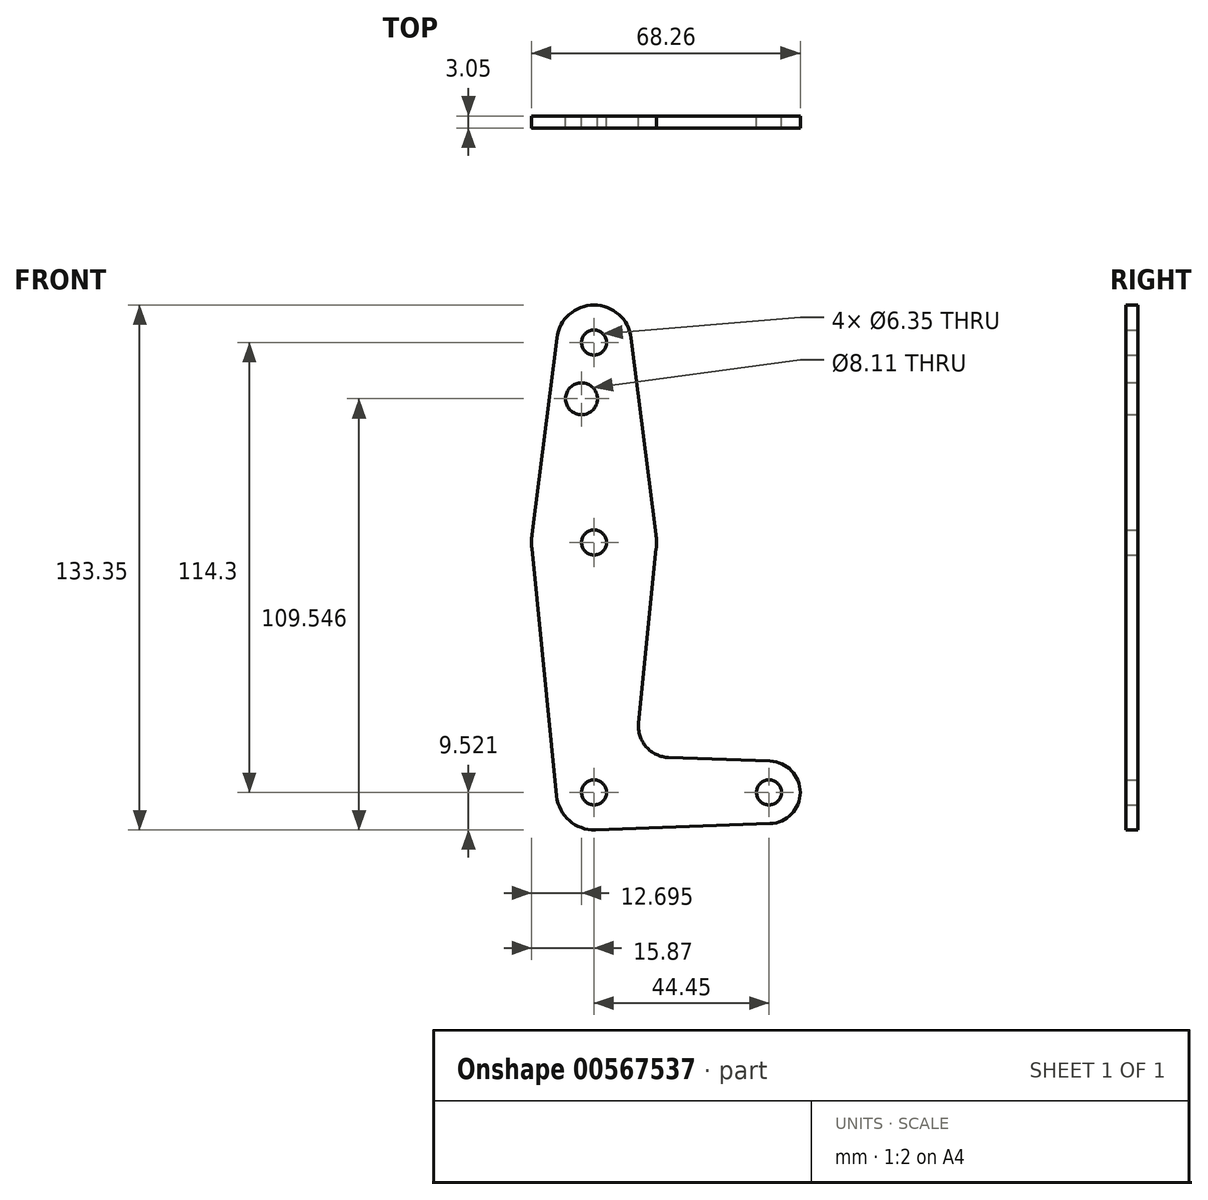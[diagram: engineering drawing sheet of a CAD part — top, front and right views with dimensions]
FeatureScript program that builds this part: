
annotation { "Feature Type Name" : "Feature", "Feature Type Description" : "" }
export const myFeature = defineFeature(function(context is Context, id is Id, definition is map)
    precondition{}
    {
        {
            var Q0;
            Q0=qCreatedBy(makeId("Front.planeOp"),FACE);
            var sketch = newSketch(context, id + "F0", { "sketchPlane" : qUnion([Q0])});
            skLineSegment(sketch, "E0", {"start": v(0, 66.21) * mm, "end": v(0, -48.09) * mm});
            skLineSegment(sketch, "E1", {"start": v(0, -48.09) * mm, "end": v(44.45, -48.09) * mm});
            skCircle(sketch, "E2", {"center": v(0, 66.21) * mm, "radius": 9.53 * mm});
            skCircle(sketch, "E3", {"center": v(0, 15.41) * mm, "radius": 15.88 * mm});
            skCircle(sketch, "E4", {"center": v(0, -48.09) * mm, "radius": 9.53 * mm});
            skCircle(sketch, "E5", {"center": v(44.45, -48.09) * mm, "radius": 7.94 * mm});
            skLineSegment(sketch, "E6", {"start": v(0.34, -57.6) * mm, "end": v(44.73, -56.02) * mm});
            skCircle(sketch, "E7", {"center": v(0, 66.21) * mm, "radius": 3.18 * mm});
            skCircle(sketch, "E8", {"center": v(-3.17, 51.94) * mm, "radius": 4.05 * mm});
            skCircle(sketch, "E9", {"center": v(0, 15.41) * mm, "radius": 3.18 * mm});
            skCircle(sketch, "E10", {"center": v(0, -48.09) * mm, "radius": 3.18 * mm});
            skCircle(sketch, "E11", {"center": v(44.45, -48.09) * mm, "radius": 3.18 * mm});
            skLineSegment(sketch, "E12", {"start": v(-9.45, 67.4) * mm, "end": v(-15.75, 17.4) * mm});
            skLineSegment(sketch, "E13", {"start": v(9.45, 67.4) * mm, "end": v(15.75, 17.4) * mm});
            skLineSegment(sketch, "E14", {"start": v(-15.8, 13.82) * mm, "end": v(-9.48, -49.04) * mm});
            skLineSegment(sketch, "E15", {"start": v(15.8, 13.82) * mm, "end": v(11.34, -30.5) * mm});
            skLineSegment(sketch, "E16", {"start": v(18.97, -39.24) * mm, "end": v(44.73, -40.16) * mm});
            skArc(sketch, "E17.filletArc", {"start": v(11.34, -30.5) * mm, "mid": v(13.26, -36.52) * mm, "end": v(18.97, -39.24) * mm});
            skSolve(sketch);
        }
        {
            var Q0;
            Q0 = qSketchRegion(id + "F0", true);
            var Q1;
            {var subQ0=sQuery(id+"F0.wireOp",EDGE,"E4");var subQ1=sQuery(id+"F0.wireOp",EDGE,"E0");var subQ2=makeQuery(id+"F0.imprint","INTERSECT",VERTEX,{"derivedFrom":[subQ1,subQ0]});Q1=makeQuery(id+"F0.imprint","IMPRINT",FACE,{"disambiguationData":[TD([[makeQuery(id+"F0.imprint","IMPRINT",EDGE,{"disambiguationData":[TD([[subQ2,-1.0]])],"derivedFrom":subQ1}),1.0]])]});}
            extrude(context, id + "F1", {"entities" : qUnion([Q0, Q1]), "depth" : 3.05 * mm, "offsetDistance" : 25.4 * mm});
        }
    });
